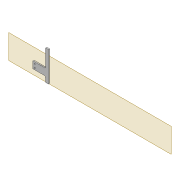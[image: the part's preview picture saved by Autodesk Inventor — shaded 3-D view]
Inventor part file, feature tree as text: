
AUTODESK INVENTOR PART (.ipt)
format: ipt  version: 2022 (Build 260153000, 153)  size: 527,360 bytes
history: native  units: mm
features: extrude x9, sketch x9, projected_geometry x9, fillet x2, shell x1, plane x1, chamfer x1
ambient origin geometry x8: Origin, YZ Plane, XZ Plane, XY Plane, X Axis, Y Axis, Z Axis, Center Point
bodies: Solid1 (feature_tree)
feature tree (32):
  extrude  "Extrusion1"  Depth=2.0mm
  shell  "Shell1"  Thickness=2.0mm
  extrude  "Extrusion8"  Depth=2.0mm
  extrude  "Extrusion3"  Depth=10.0mm TaperAngle=0.0deg
  extrude  "Extrusion4"  Depth=2.0mm
  fillet  "Fillet1"  Radius=5.0mm
  sketch  "Sketch10"  dims[d22=2.0mm d23=0.0mm d31=2.0mm d32=5.0mm]
  extrude  "Extrusion5"  Depth=2.5mm
  plane  "Work Plane2"
  extrude  "Extrusion9"  Depth=5.0mm
  extrude  "Extrusion10"  Depth=80.0mm
  fillet  "Fillet2"  Radius=6.0mm
  extrude  "Extrusion11"  Depth=2.0mm
  chamfer  "Chamfer1"  Distance=5.0mm
  extrude  "Extrusion13"  Depth=22.0mm
  sketch  "Sketch30"  dims[d64=2.0mm d65=0.0mm d66=3.0mm]
  sketch  "Sketch31"  dims[d67=12.0mm d68=5.0mm d69=22.0mm d70=12.0mm d71=3.05mm d72=2.0mm d73=0.0mm d74=10.0mm d75=0.0mm d76=2.0mm d77=100.0mm d78=20.0mm d79=0.5mm d80=10.0mm d81=0.0mm d84=10.0mm d85=10.0mm d87=3.0mm d88=2.0mm d89=45.0deg d90=1.0mm d91=1.0mm d92=1.0mm d93=1.0mm d94=1.0mm d95=1.0mm d96=10.0mm d97=0.0mm]
  sketch  "Sketch3"  dims[d0=2.0mm d1=0.0mm d2=4.0mm d7=2.0mm]
  sketch  "Sketch8"  dims[d8=2.0mm d9=5.9mm]
  sketch  "Sketch9"  dims[d13=10.0mm d14=0.0mm d16=10.0mm d17=0.0mm]
  projected_geometry  "Projected Loop4"
  projected_geometry  "Projected Loop10"
  sketch  "Sketch24"  dims[d34=1.6mm d35=2.5mm]
  projected_geometry  "Projected Loop11"
  projected_geometry  "Projected Loop12"
  sketch  "Sketch26"  dims[d37=5.0mm d38=1.6mm]
  projected_geometry  "Projected Loop13"
  sketch  "Sketch29"  dims[d40=2.5mm d62=80.0mm d63=6.0mm]
  projected_geometry  "Project Cut Edges1"
  projected_geometry  "Project Cut Edges3"
  projected_geometry  "Project Cut Edges4"
  projected_geometry  "Project Cut Edges5"
